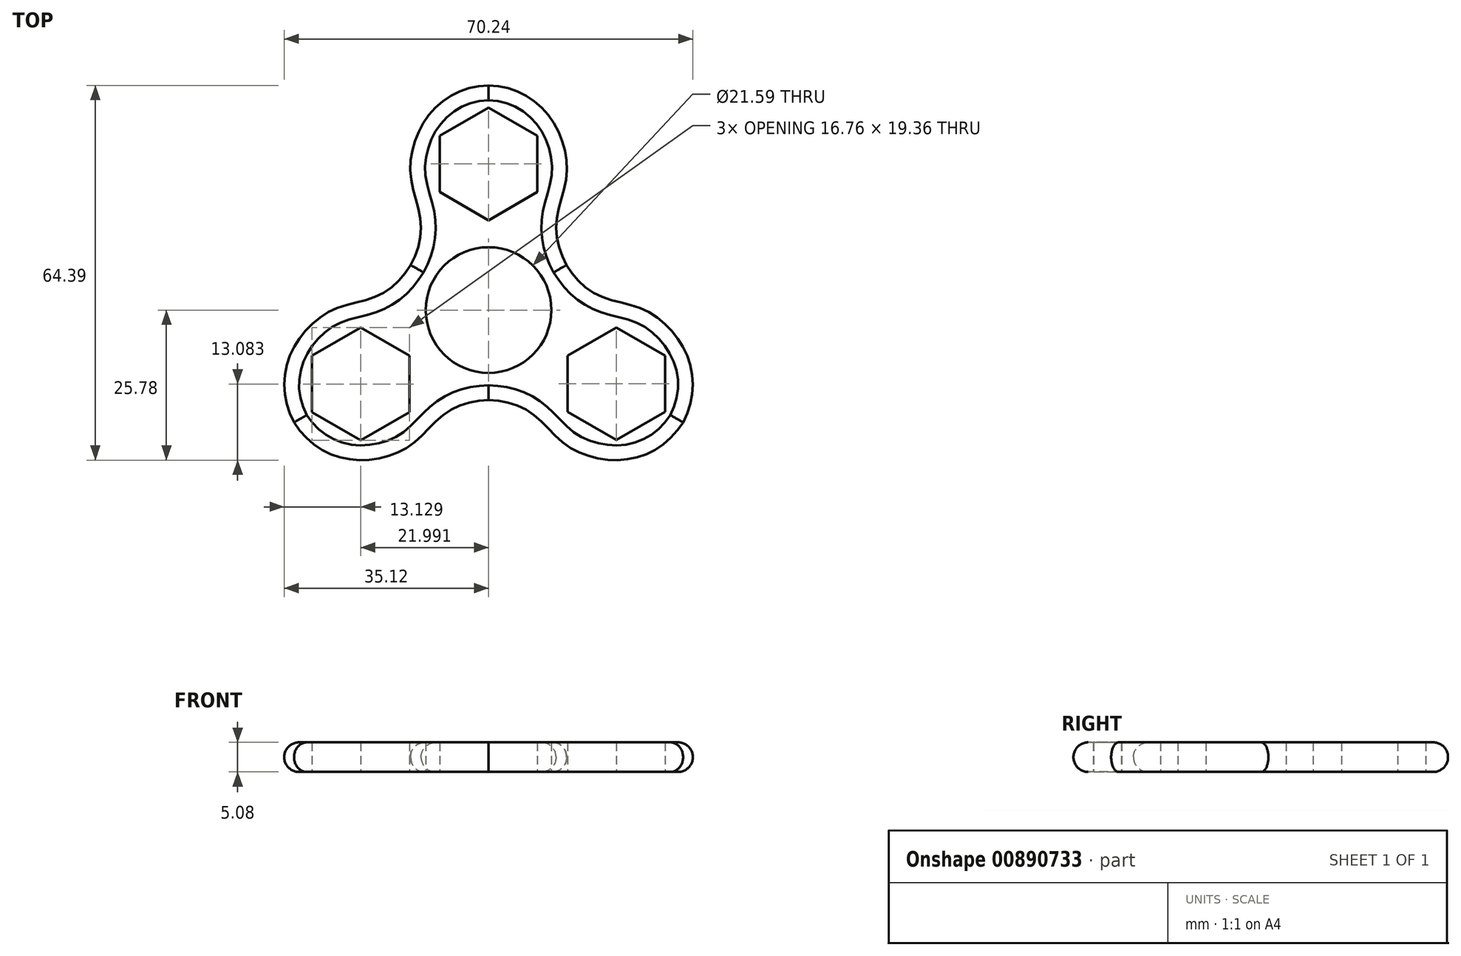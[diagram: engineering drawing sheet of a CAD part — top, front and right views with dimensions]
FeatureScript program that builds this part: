
annotation { "Feature Type Name" : "Feature", "Feature Type Description" : "" }
export const myFeature = defineFeature(function(context is Context, id is Id, definition is map)
    precondition{}
    {
        {
            var Q0;
            Q0=qCreatedBy(makeId("Top.planeOp"),FACE);
            var sketch = newSketch(context, id + "F0", { "sketchPlane" : qUnion([Q0])});
            skCircle(sketch, "E0", {"center": v(0, 0) * mm, "radius": 10.8 * mm});
            skLineSegment(sketch, "E1", {"start": v(0, 0) * mm, "end": v(0, 25.1) * mm, "construction": true});
            skLineSegment(sketch, "E2", {"start": v(0, 0) * mm, "end": v(21.74, 12.55) * mm, "construction": true});
            skLineSegment(sketch, "E3", {"start": v(0, 0) * mm, "end": v(21.94, -12.67) * mm, "construction": true});
            skLineSegment(sketch, "E4", {"start": v(0, 0) * mm, "end": v(0, -25.1) * mm, "construction": true});
            skLineSegment(sketch, "E5", {"start": v(0, 0) * mm, "end": v(-22, -12.7) * mm, "construction": true});
            skLineSegment(sketch, "E6", {"start": v(0, 0) * mm, "end": v(-21.74, 12.55) * mm, "construction": true});
            skCircle(sketch, "E7.cCircle", {"center": v(0, 25.1) * mm, "radius": 8.38 * mm, "construction": true});
            skLineSegment(sketch, "E7.0", {"start": v(8.38, 29.95) * mm, "end": v(8.38, 20.27) * mm});
            skLineSegment(sketch, "E7.1", {"start": v(8.38, 20.27) * mm, "end": v(0, 15.43) * mm});
            skLineSegment(sketch, "E7.2", {"start": v(0, 15.43) * mm, "end": v(-8.38, 20.27) * mm});
            skLineSegment(sketch, "E7.3", {"start": v(-8.38, 20.27) * mm, "end": v(-8.38, 29.95) * mm});
            skLineSegment(sketch, "E7.4", {"start": v(-8.38, 29.95) * mm, "end": v(0, 34.79) * mm});
            skLineSegment(sketch, "E7.5", {"start": v(0, 34.79) * mm, "end": v(8.38, 29.95) * mm});
            skPoint(sketch, "E7.0.midPoint", {"position": v(8.38, 25.1) * mm});
            skCircle(sketch, "E8.cCircle", {"center": v(21.94, -12.67) * mm, "radius": 8.38 * mm, "construction": true});
            skLineSegment(sketch, "E8.0", {"start": v(13.55, -17.5) * mm, "end": v(13.55, -7.83) * mm});
            skLineSegment(sketch, "E8.1", {"start": v(13.55, -7.83) * mm, "end": v(21.94, -2.99) * mm});
            skLineSegment(sketch, "E8.2", {"start": v(21.94, -2.99) * mm, "end": v(30.32, -7.83) * mm});
            skLineSegment(sketch, "E8.3", {"start": v(30.32, -7.83) * mm, "end": v(30.32, -17.5) * mm});
            skLineSegment(sketch, "E8.4", {"start": v(30.32, -17.5) * mm, "end": v(21.94, -22.34) * mm});
            skLineSegment(sketch, "E8.5", {"start": v(21.94, -22.34) * mm, "end": v(13.55, -17.5) * mm});
            skPoint(sketch, "E8.0.midPoint", {"position": v(13.55, -12.67) * mm});
            skCircle(sketch, "E9.cCircle", {"center": v(-22, -12.7) * mm, "radius": 8.38 * mm, "construction": true});
            skLineSegment(sketch, "E9.0", {"start": v(-13.6, -7.86) * mm, "end": v(-13.6, -17.54) * mm});
            skLineSegment(sketch, "E9.1", {"start": v(-13.6, -17.54) * mm, "end": v(-22, -22.38) * mm});
            skLineSegment(sketch, "E9.2", {"start": v(-22, -22.38) * mm, "end": v(-30.37, -17.54) * mm});
            skLineSegment(sketch, "E9.3", {"start": v(-30.37, -17.54) * mm, "end": v(-30.37, -7.86) * mm});
            skLineSegment(sketch, "E9.4", {"start": v(-30.37, -7.86) * mm, "end": v(-22, -3.02) * mm});
            skLineSegment(sketch, "E9.5", {"start": v(-22, -3.02) * mm, "end": v(-13.6, -7.86) * mm});
            skPoint(sketch, "E9.0.midPoint", {"position": v(-13.6, -12.7) * mm});
            skFitSpline(sketch, "E10", {"points": [v(0, 38.6) * mm, v(13.45, 23.73) * mm, v(13.39, 7.73) * mm], "startDerivative": vector(54.84, -2.13) * mm, "endDerivative": vector(24.96, -47.54) * mm});
            skFitSpline(sketch, "E11.MirrorCS", {"points": [v(33.44, -19.3) * mm, v(27.28, -0.22) * mm, v(13.39, 7.73) * mm], "startDerivative": vector(25.58, 48.55) * mm, "endDerivative": vector(-28.7, 45.38) * mm});
            skFitSpline(sketch, "E12.MirrorCS", {"points": [v(33.44, -19.3) * mm, v(13.83, -23.51) * mm, v(0, -15.46) * mm], "startDerivative": vector(-29.26, -46.43) * mm, "endDerivative": vector(-53.65, 2.16) * mm});
            skFitSpline(sketch, "E13.MirrorCS", {"points": [v(-33.44, -19.3) * mm, v(-13.83, -23.51) * mm, v(0, -15.46) * mm], "startDerivative": vector(29.26, -46.43) * mm, "endDerivative": vector(53.65, 2.16) * mm});
            skFitSpline(sketch, "E14.MirrorCS", {"points": [v(-33.44, -19.3) * mm, v(-27.28, -0.22) * mm, v(-13.39, 7.73) * mm], "startDerivative": vector(-25.58, 48.55) * mm, "endDerivative": vector(28.7, 45.38) * mm});
            skFitSpline(sketch, "E15.MirrorCS", {"points": [v(0, 38.6) * mm, v(-13.45, 23.73) * mm, v(-13.39, 7.73) * mm], "startDerivative": vector(-54.84, -2.13) * mm, "endDerivative": vector(-24.96, -47.54) * mm});
            skSolve(sketch);
        }
        {
            var Q0;
            Q0=makeQuery(id+"F0.imprint","IMPRINT",FACE,{"disambiguationData":[TD([[makeQuery(id+"F0.imprint","IMPRINT",EDGE,{"derivedFrom":sQuery(id+"F0.wireOp",EDGE,"E0")}),-1.0]])]});
            extrude(context, id + "F1", {"entities" : qUnion([Q0]), "endBound" : BoundingType.SYMMETRIC, "depth" : 5.08 * mm, "offsetDistance" : 25.4 * mm});
        }
        {
            var Q0;
            Q0=makeQuery(id+"F1.opExtrude","CAP_EDGE",EDGE,{"disambiguationData":[OSD([sQuery(id+"F0.wireOp",EDGE,"E13.MirrorCS")])],"isStart":false});
            var Q1;
            Q1=makeQuery(id+"F1.opExtrude","CAP_EDGE",EDGE,{"disambiguationData":[OSD([sQuery(id+"F0.wireOp",EDGE,"E12.MirrorCS")])],"isStart":false});
            var Q2;
            Q2=makeQuery(id+"F1.opExtrude","CAP_EDGE",EDGE,{"disambiguationData":[OSD([sQuery(id+"F0.wireOp",EDGE,"E11.MirrorCS")])],"isStart":false});
            var Q3;
            Q3=makeQuery(id+"F1.opExtrude","CAP_EDGE",EDGE,{"disambiguationData":[OSD([sQuery(id+"F0.wireOp",EDGE,"E10")])],"isStart":false});
            var Q4;
            Q4=makeQuery(id+"F1.opExtrude","CAP_EDGE",EDGE,{"disambiguationData":[OSD([sQuery(id+"F0.wireOp",EDGE,"E15.MirrorCS")])],"isStart":false});
            var Q5;
            Q5=makeQuery(id+"F1.opExtrude","CAP_EDGE",EDGE,{"disambiguationData":[OSD([sQuery(id+"F0.wireOp",EDGE,"E14.MirrorCS")])],"isStart":false});
            var Q6;
            Q6=makeQuery(id+"F1.opExtrude","CAP_EDGE",EDGE,{"disambiguationData":[OSD([sQuery(id+"F0.wireOp",EDGE,"E13.MirrorCS")])],"isStart":true});
            var Q7;
            Q7=makeQuery(id+"F1.opExtrude","CAP_EDGE",EDGE,{"disambiguationData":[OSD([sQuery(id+"F0.wireOp",EDGE,"E12.MirrorCS")])],"isStart":true});
            var Q8;
            Q8=makeQuery(id+"F1.opExtrude","CAP_EDGE",EDGE,{"disambiguationData":[OSD([sQuery(id+"F0.wireOp",EDGE,"E11.MirrorCS")])],"isStart":true});
            var Q9;
            Q9=makeQuery(id+"F1.opExtrude","CAP_EDGE",EDGE,{"disambiguationData":[OSD([sQuery(id+"F0.wireOp",EDGE,"E10")])],"isStart":true});
            var Q10;
            Q10=makeQuery(id+"F1.opExtrude","CAP_EDGE",EDGE,{"disambiguationData":[OSD([sQuery(id+"F0.wireOp",EDGE,"E15.MirrorCS")])],"isStart":true});
            var Q11;
            Q11=makeQuery(id+"F1.opExtrude","CAP_EDGE",EDGE,{"disambiguationData":[OSD([sQuery(id+"F0.wireOp",EDGE,"E14.MirrorCS")])],"isStart":true});
            fillet(context, id + "F2", {"entities" : qUnion([Q0, Q1, Q2, Q3, Q4, Q5, Q6, Q7, Q8, Q9, Q10, Q11]), "radius" : 2.54 * mm, "tangentPropagation" : true, "allowEdgeOverflow" : false});
        }
    });
